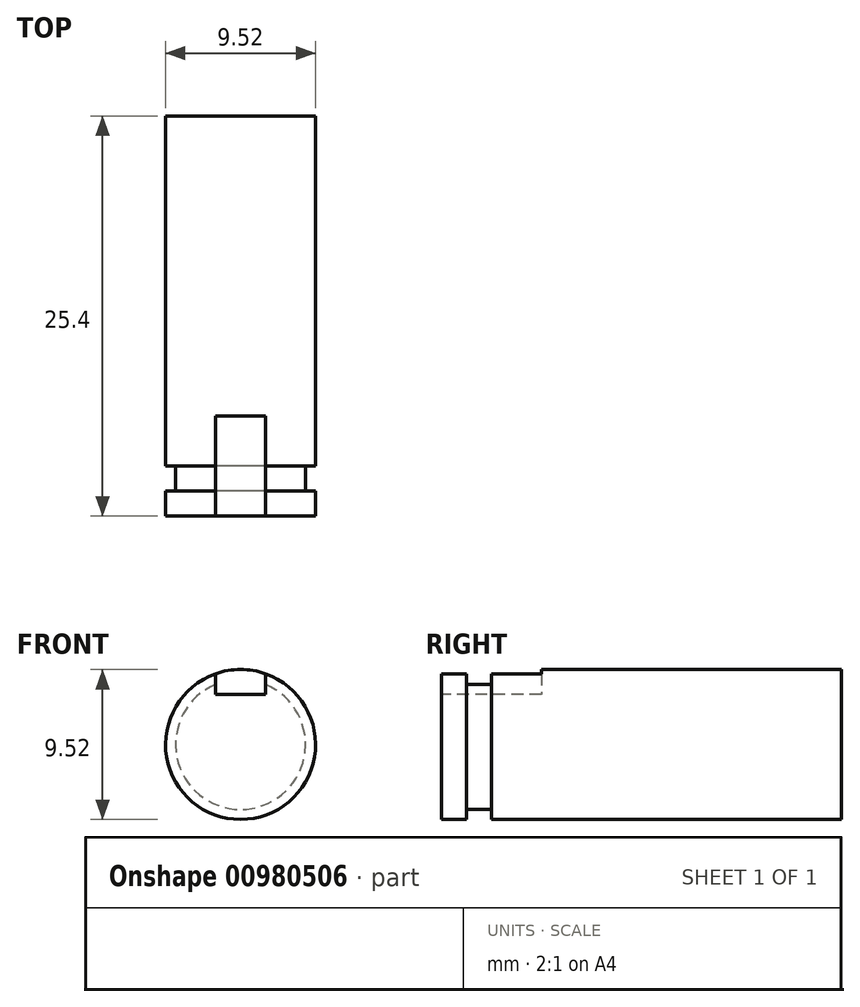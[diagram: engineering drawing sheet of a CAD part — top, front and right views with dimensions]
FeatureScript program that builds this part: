
annotation { "Feature Type Name" : "Feature", "Feature Type Description" : "" }
export const myFeature = defineFeature(function(context is Context, id is Id, definition is map)
    precondition{}
    {
        {
            var Q0;
            Q0=qCreatedBy(makeId("Front.planeOp"),FACE);
            var sketch = newSketch(context, id + "F0", { "sketchPlane" : qUnion([Q0])});
            skCircle(sketch, "E0", {"center": v(0, 0) * mm, "radius": 4.76 * mm});
            skSolve(sketch);
        }
        {
            var Q0;
            Q0 = qSketchRegion(id + "F0", true);
            extrude(context, id + "F1", {"entities" : qUnion([Q0]), "depth" : 25.4 * mm, "offsetDistance" : 25.4 * mm});
        }
        {
            var Q0;
            Q0=makeQuery(id+"F1.opExtrude","CAP_FACE",FACE,{"disambiguationData":[OSD([sQuery(id+"F0.wireOp",EDGE,"E0")])],"isStart":false});
            var sketch = newSketch(context, id + "F2", { "sketchPlane" : qUnion([Q0])});
            skLineSegment(sketch, "E1.bottom", {"start": v(-1.59, 6.35) * mm, "end": v(1.59, 6.35) * mm});
            skLineSegment(sketch, "E1.top", {"start": v(-1.59, 3.17) * mm, "end": v(1.59, 3.18) * mm});
            skLineSegment(sketch, "E1.left", {"start": v(-1.59, 6.35) * mm, "end": v(-1.59, 3.17) * mm});
            skLineSegment(sketch, "E1.right", {"start": v(1.59, 6.35) * mm, "end": v(1.59, 3.18) * mm});
            skLineSegment(sketch, "E2", {"start": v(0, 0) * mm, "end": v(0, 3.18) * mm, "construction": true});
            skLineSegment(sketch, "E3", {"start": v(-1.59, 4.76) * mm, "end": v(1.59, 4.76) * mm, "construction": true});
            skSolve(sketch);
        }
        {
            var Q0;
            Q0 = qSketchRegion(id + "F2", true);
            extrude(context, id + "F3", {"entities" : qUnion([Q0]), "operationType" : NewBodyOperationType.REMOVE, "oppositeDirection" : true, "depth" : 6.35 * mm, "offsetDistance" : 25.4 * mm});
        }
        {
            var Q0;
            Q0=makeQuery(id+"F1.opExtrude","CAP_FACE",FACE,{"disambiguationData":[OSD([sQuery(id+"F0.wireOp",EDGE,"E0")])],"isStart":true});
            var Q1;
            Q1=makeQuery(id+"F1.opExtrude","CAP_FACE",FACE,{"disambiguationData":[OSD([sQuery(id+"F0.wireOp",EDGE,"E0")])],"isStart":false});
            cPlane(context, id + "F4", {"entities" : qUnion([Q0, Q1]), "cplaneType" : CPlaneType.MID_PLANE, "offset" : 25.4 * mm, "width" : 152.4 * mm, "height" : 152.4 * mm});
        }
        {
            var Q0;
            Q0=qCreatedBy(makeId("Right.planeOp"),FACE);
            var sketch = newSketch(context, id + "F5", { "sketchPlane" : qUnion([Q0])});
            skLineSegment(sketch, "E4", {"start": v(-22.23, -4.76) * mm, "end": v(-23.81, -4.76) * mm});
            skLineSegment(sketch, "E5", {"start": v(-23.81, -4.76) * mm, "end": v(-22.23, -4.76) * mm});
            skLineSegment(sketch, "E6", {"start": v(-22.23, -4.76) * mm, "end": v(-22.23, -4.13) * mm});
            skLineSegment(sketch, "E7", {"start": v(-22.23, -4.13) * mm, "end": v(-23.81, -4.13) * mm});
            skLineSegment(sketch, "E8", {"start": v(-23.81, -4.13) * mm, "end": v(-23.81, -4.76) * mm});
            skLineSegment(sketch, "E9", {"start": v(-25.38, 0) * mm, "end": v(0, 0) * mm, "construction": true});
            skSolve(sketch);
        }
        {
            var Q0;
            Q0 = qSketchRegion(id + "F5", true);
            var Q1;
            Q1=sQuery(id+"F5.wireOp",EDGE,"E9");
            revolve(context, id + "F6", {"operationType" : NewBodyOperationType.REMOVE, "surfaceOperationType" : NewSurfaceOperationType.NEW, "entities" : qUnion([Q0]), "axis" : qUnion([Q1]), "revolveType" : RevolveType.FULL, "oppositeDirection" : true});
        }
    });
